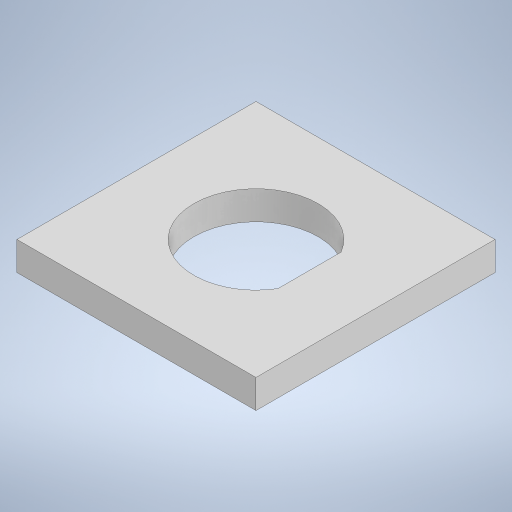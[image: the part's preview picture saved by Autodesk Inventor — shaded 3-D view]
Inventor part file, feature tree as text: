
AUTODESK INVENTOR PART (.ipt)
format: ipt  version: 2024.2 (Build 282272000, 272)  size: 216,576 bytes
history: native  units: mm
features: extrude x1, sketch x1
ambient origin geometry x8: Origin, YZ Plane, XZ Plane, XY Plane, X Axis, Y Axis, Z Axis, Center Point
bodies: Solid1 (feature_tree)
feature tree (2):
  extrude  "Extrusion1"  Depth=25.0mm
  sketch  "Sketch1"  dims[d0=13.0mm d1=25.0mm d2=25.0mm d3=12.5mm d4=12.5mm d5=3.0mm d6=0.0mm d7=5.6mm]
